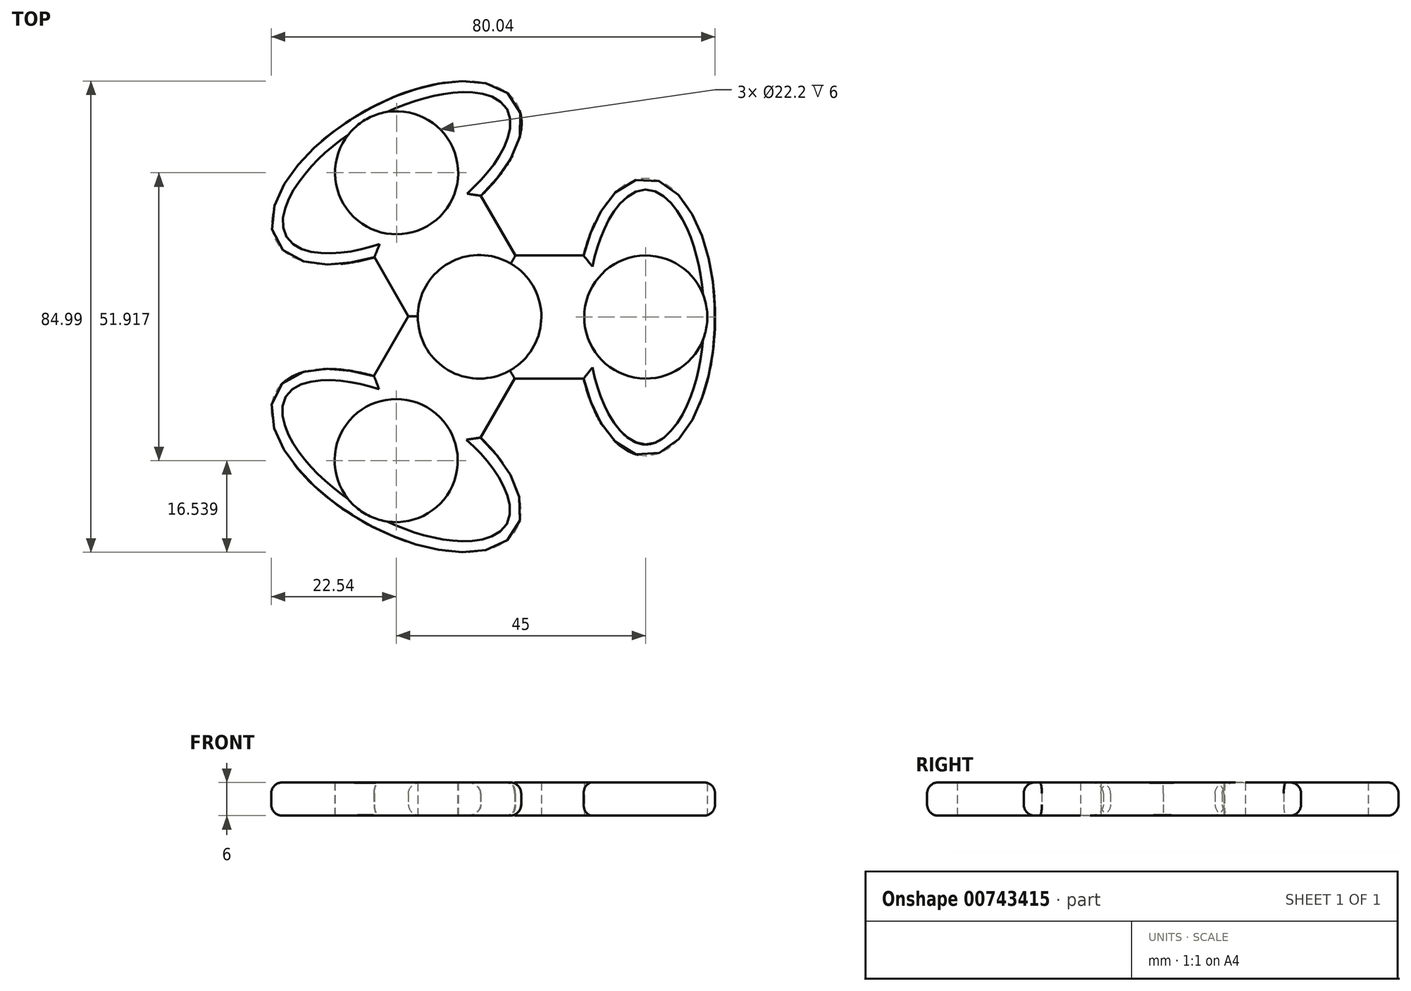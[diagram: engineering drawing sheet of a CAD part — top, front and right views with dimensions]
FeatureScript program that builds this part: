
annotation { "Feature Type Name" : "Feature", "Feature Type Description" : "" }
export const myFeature = defineFeature(function(context is Context, id is Id, definition is map)
    precondition{}
    {
        {
            var Q0;
            Q0=qCreatedBy(makeId("Top.planeOp"),FACE);
            var sketch = newSketch(context, id + "F0", { "sketchPlane" : qUnion([Q0])});
            skCircle(sketch, "E0", {"center": v(0, 0) * mm, "radius": 11.1 * mm});
            skLineSegment(sketch, "E1", {"start": v(0, 0) * mm, "end": v(30, 0) * mm});
            skCircle(sketch, "E2", {"center": v(30, 0) * mm, "radius": 11.1 * mm});
            skLineSegment(sketch, "E3", {"start": v(0, 11.1) * mm, "end": v(30, 11.1) * mm});
            skLineSegment(sketch, "E4", {"start": v(0, -11.1) * mm, "end": v(30, -11.1) * mm});
            skEllipse(sketch, "E5", {"center": v(30, 0) * mm, "majorRadius": 25 * mm, "minorRadius": 12.5 * mm, "majorAxis": v(0, 1)});
            skLineSegment(sketch, "E6.1.0", {"start": v(-9.53, -5.5) * mm, "end": v(-24.53, 20.48) * mm});
            skEllipse(sketch, "E6.1.1", {"center": v(-14.92, 26.03) * mm, "majorRadius": 25 * mm, "minorRadius": 12.5 * mm, "majorAxis": v(-0.87, -0.5)});
            skLineSegment(sketch, "E6.1.2", {"start": v(0.08, 0.05) * mm, "end": v(-14.92, 26.03) * mm});
            skLineSegment(sketch, "E6.1.3", {"start": v(9.7, 5.6) * mm, "end": v(-5.3, 31.58) * mm});
            skCircle(sketch, "E6.1.4", {"center": v(0.08, 0.04) * mm, "radius": 11.1 * mm});
            skCircle(sketch, "E6.1.5", {"center": v(-14.92, 26.03) * mm, "radius": 11.1 * mm});
            skLineSegment(sketch, "E6.2.0", {"start": v(9.61, -5.46) * mm, "end": v(-5.39, -31.44) * mm});
            skEllipse(sketch, "E6.2.1", {"center": v(-15, -25.9) * mm, "majorRadius": 25 * mm, "minorRadius": 12.5 * mm, "majorAxis": v(0.87, -0.5)});
            skLineSegment(sketch, "E6.2.2", {"start": v(0, 0.09) * mm, "end": v(-15, -25.9) * mm});
            skLineSegment(sketch, "E6.2.3", {"start": v(-9.61, 5.64) * mm, "end": v(-24.61, -20.34) * mm});
            skCircle(sketch, "E6.2.4", {"center": v(0, 0.09) * mm, "radius": 11.1 * mm});
            skCircle(sketch, "E6.2.5", {"center": v(-15, -25.9) * mm, "radius": 11.1 * mm});
            skPoint(sketch, "E6.center", {"position": v(0.03, 0.04) * mm});
            skSolve(sketch);
        }
        {
            var Q0;
            Q0 = qSketchRegion(id + "F0", true);
            extrude(context, id + "F1", {"entities" : qUnion([Q0]), "depth" : 6 * mm, "offsetDistance" : 25 * mm});
        }
        {
            var Q0;
            Q0=makeQuery(id+"F1.opExtrude","CAP_EDGE",EDGE,{"disambiguationData":[OSD([sQuery(id+"F0.wireOp",EDGE,"E5")])],"isStart":false});
            var Q1;
            Q1=makeQuery(id+"F1.opExtrude","CAP_EDGE",EDGE,{"disambiguationData":[OSD([sQuery(id+"F0.wireOp",EDGE,"E4")])],"isStart":false});
            var Q2;
            Q2=makeQuery(id+"F1.opExtrude","CAP_EDGE",EDGE,{"disambiguationData":[OSD([sQuery(id+"F0.wireOp",EDGE,"E6.2.1")])],"isStart":false});
            var Q3;
            Q3=makeQuery(id+"F1.opExtrude","CAP_EDGE",EDGE,{"disambiguationData":[OSD([sQuery(id+"F0.wireOp",EDGE,"E6.2.3")])],"isStart":false});
            var Q4;
            Q4=makeQuery(id+"F1.opExtrude","CAP_EDGE",EDGE,{"disambiguationData":[OSD([sQuery(id+"F0.wireOp",EDGE,"E6.1.0")])],"isStart":false});
            var Q5;
            Q5=makeQuery(id+"F1.opExtrude","CAP_EDGE",EDGE,{"disambiguationData":[OSD([sQuery(id+"F0.wireOp",EDGE,"E6.1.1")])],"isStart":false});
            var Q6;
            Q6=makeQuery(id+"F1.opExtrude","CAP_EDGE",EDGE,{"disambiguationData":[OSD([sQuery(id+"F0.wireOp",EDGE,"E6.1.3")])],"isStart":false});
            var Q7;
            Q7=makeQuery(id+"F1.opExtrude","CAP_EDGE",EDGE,{"disambiguationData":[OSD([sQuery(id+"F0.wireOp",EDGE,"E3")])],"isStart":false});
            var Q8;
            Q8=makeQuery(id+"F1.opExtrude","CAP_EDGE",EDGE,{"disambiguationData":[OSD([sQuery(id+"F0.wireOp",EDGE,"E6.2.0")])],"isStart":false});
            fillet(context, id + "F2", {"entities" : qUnion([Q0, Q1, Q2, Q3, Q4, Q5, Q6, Q7, Q8]), "radius" : 2 * mm, "tangentPropagation" : true, "allowEdgeOverflow" : false});
        }
        {
            var Q0;
            Q0=makeQuery(id+"F1.opExtrude","CAP_EDGE",EDGE,{"disambiguationData":[OSD([sQuery(id+"F0.wireOp",EDGE,"E5")])],"isStart":true});
            fillet(context, id + "F3", {"entities" : qUnion([Q0]), "radius" : 2 * mm, "tangentPropagation" : true, "allowEdgeOverflow" : false});
        }
        {
            var Q0;
            Q0=makeQuery(id+"F1.opExtrude","CAP_EDGE",EDGE,{"disambiguationData":[OSD([sQuery(id+"F0.wireOp",EDGE,"E3")])],"isStart":true});
            var Q1;
            Q1=makeQuery(id+"F1.opExtrude","CAP_EDGE",EDGE,{"disambiguationData":[OSD([sQuery(id+"F0.wireOp",EDGE,"E4")])],"isStart":true});
            var Q2;
            Q2=makeQuery(id+"F1.opExtrude","CAP_EDGE",EDGE,{"disambiguationData":[OSD([sQuery(id+"F0.wireOp",EDGE,"E6.2.3")])],"isStart":true});
            var Q3;
            Q3=makeQuery(id+"F1.opExtrude","CAP_EDGE",EDGE,{"disambiguationData":[OSD([sQuery(id+"F0.wireOp",EDGE,"E6.2.0")])],"isStart":true});
            var Q4;
            Q4=makeQuery(id+"F1.opExtrude","CAP_EDGE",EDGE,{"disambiguationData":[OSD([sQuery(id+"F0.wireOp",EDGE,"E6.1.0")])],"isStart":true});
            var Q5;
            Q5=makeQuery(id+"F1.opExtrude","CAP_EDGE",EDGE,{"disambiguationData":[OSD([sQuery(id+"F0.wireOp",EDGE,"E6.1.3")])],"isStart":true});
            fillet(context, id + "F4", {"entities" : qUnion([Q0, Q1, Q2, Q3, Q4, Q5]), "radius" : 2 * mm, "tangentPropagation" : true, "allowEdgeOverflow" : false});
        }
        {
            var Q0;
            Q0=makeQuery(id+"F1.opExtrude","CAP_EDGE",EDGE,{"disambiguationData":[OSD([sQuery(id+"F0.wireOp",EDGE,"E6.1.1")])],"isStart":true});
            var Q1;
            Q1=makeQuery(id+"F1.opExtrude","CAP_EDGE",EDGE,{"disambiguationData":[OSD([sQuery(id+"F0.wireOp",EDGE,"E6.2.1")])],"isStart":true});
            fillet(context, id + "F5", {"entities" : qUnion([Q0, Q1]), "radius" : 2 * mm, "tangentPropagation" : true, "allowEdgeOverflow" : false});
        }
    });
